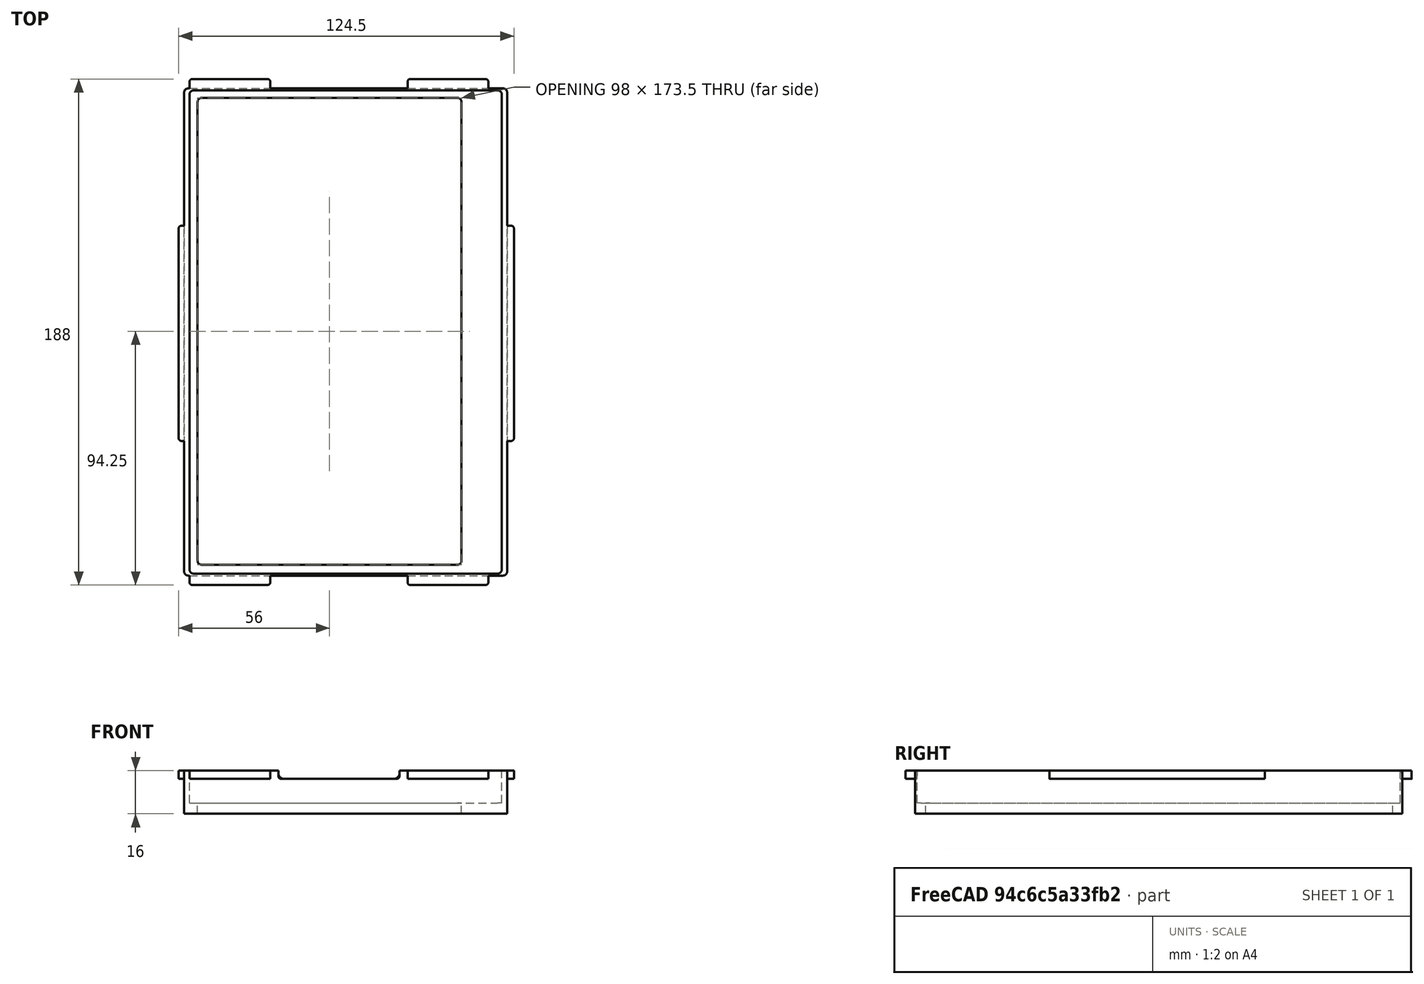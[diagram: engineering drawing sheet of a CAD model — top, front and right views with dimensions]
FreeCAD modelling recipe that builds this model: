
FCSTD DOCUMENT  (FreeCAD 0.20R29177 (Git))
Label: carrier-atoto-s8_test_i
License: All rights reserved
LicenseURL: http://en.wikipedia.org/wiki/All_rights_reserved
objects: Part::Box×12, Part::Fillet×11, Part::MultiFuse×4, Part::Cut×3
note: 30 computed .brp shape members not serialized (recipe doc carries the construction recipe); baked Part::Feature solids carry a one-line shape summary decoded from their .brp

FEATURE [Part::Box] Box  label="Cube"
  AttacherType = Attacher::AttachEngine3D
  Height = 4
  Length = 120
  Placement = pos=(2,0,0) rot=(0,0,1;0rad)
  Width = 181
FEATURE [Part::Box] Box001  label="Cube001"
  AttacherType = Attacher::AttachEngine3D
  Height = 4
  Length = 98
  Placement = pos=(7,4,0) rot=(0,0,1;0rad)
  Width = 173.5
FEATURE [Part::Fillet] Fillet
  Base = -> Box001
  Edges = 4 edges r=1.5: [Edge1,Edge3,Edge5,Edge7]
FEATURE [Part::Fillet] Fillet001
  Base = -> Box
  Edges = 4 edges r=1.5: [Edge1,Edge3,Edge5,Edge7]
FEATURE [Part::Cut] Cut
  Base = -> Fillet001
  Tool = -> Fillet
FEATURE [Part::Box] Box002  label="Cube002"
  AttacherType = Attacher::AttachEngine3D
  Height = 12
  Length = 120
  Placement = pos=(2,0,4) rot=(0,0,1;0rad)
  Width = 181
FEATURE [Part::Box] Box003  label="Cube003"
  AttacherType = Attacher::AttachEngine3D
  Height = 20
  Length = 116
  Placement = pos=(4,0.75,4) rot=(0,0,1;0rad)
  Width = 179.5
FEATURE [Part::Fillet] Fillet002
  Base = -> Box003
  Edges = 4 edges r=1.5: [Edge1,Edge3,Edge5,Edge7]
FEATURE [Part::Fillet] Fillet003
  Base = -> Box002
  Edges = 4 edges r=1.5: [Edge1,Edge3,Edge5,Edge7]
FEATURE [Part::Cut] Cut001
  Base = -> Fillet003
  Tool = -> Fillet002
FEATURE [Part::Box] Box006  label="Cube006"
  AttacherType = Attacher::AttachEngine3D
  Height = 10
  Length = 45
  Placement = pos=(15,-5,0) rot=(0,0,1;0rad)
  Width = 10
FEATURE [Part::Box] Box007  label="Cube007"
  AttacherType = Attacher::AttachEngine3D
  Height = 10
  Length = 45
  Placement = pos=(15,175,0) rot=(0,0,1;0rad)
  Width = 10
FEATURE [Part::MultiFuse] Fusion
  Placement = pos=(22,0,13) rot=(0,0,1;0rad)
  Shapes = -> [Box007,Box006]
FEATURE [Part::Fillet] Fillet004
  Base = -> Fusion
  Edges = 4 edges: [Edge4 r=2,Edge8 r=2,Edge16 r=1,Edge20 r=1]
FEATURE [Part::Cut] Cut002
  Base = -> Cut001
  Tool = -> Fillet004
FEATURE [Part::MultiFuse] Fusion001
  Shapes = -> [Cut,Cut002]
FEATURE [Part::Box] Box008  label="Cube008"
  AttacherType = Attacher::AttachEngine3D
  Height = 3
  Length = 30
  Placement = pos=(85,180.5,5) rot=(0,0,1;0rad)
  Width = 4
FEATURE [Part::Box] Box009  label="Cube009"
  AttacherType = Attacher::AttachEngine3D
  Height = 3
  Length = 30
  Placement = pos=(4,180.5,5) rot=(0,0,1;0rad)
  Width = 4
FEATURE [Part::Box] Box010  label="Cube010"
  AttacherType = Attacher::AttachEngine3D
  Height = 3
  Length = 30
  Placement = pos=(85,-3.5,5) rot=(0,0,1;0rad)
  Width = 4
FEATURE [Part::Box] Box011  label="Cube011"
  AttacherType = Attacher::AttachEngine3D
  Height = 3
  Length = 4
  Placement = pos=(0,50,5) rot=(0,0,1;0rad)
  Width = 80
FEATURE [Part::Box] Box012  label="Cube012"
  AttacherType = Attacher::AttachEngine3D
  Height = 3
  Length = 30
  Placement = pos=(4,-3.5,5) rot=(0,0,1;0rad)
  Width = 4
FEATURE [Part::Box] Box013  label="Cube013"
  AttacherType = Attacher::AttachEngine3D
  Height = 3
  Length = 4
  Placement = pos=(120.5,50,5) rot=(0,0,1;0rad)
  Width = 80
FEATURE [Part::Fillet] Fillet005
  Base = -> Box012
  Edges = 2 edges r=1: [Edge1,Edge5]
FEATURE [Part::Fillet] Fillet006
  Base = -> Box011
  Edges = 2 edges r=1: [Edge1,Edge3]
FEATURE [Part::Fillet] Fillet007
  Base = -> Box010
  Edges = 2 edges r=1: [Edge1,Edge5]
FEATURE [Part::Fillet] Fillet008
  Base = -> Box009
  Edges = 2 edges r=1: [Edge3,Edge7]
FEATURE [Part::Fillet] Fillet009
  Base = -> Box008
  Edges = 2 edges r=1: [Edge3,Edge7]
FEATURE [Part::Fillet] Fillet010
  Base = -> Box013
  Edges = 2 edges r=1: [Edge5,Edge7]
FEATURE [Part::MultiFuse] Fusion002
  Placement = pos=(0,0,8) rot=(0,0,1;0rad)
  Shapes = -> [Fillet005,Fillet006,Fillet007,Fillet008,Fillet009,Fillet010]
FEATURE [Part::MultiFuse] Fusion003
  Shapes = -> [Fusion001,Fusion002]
